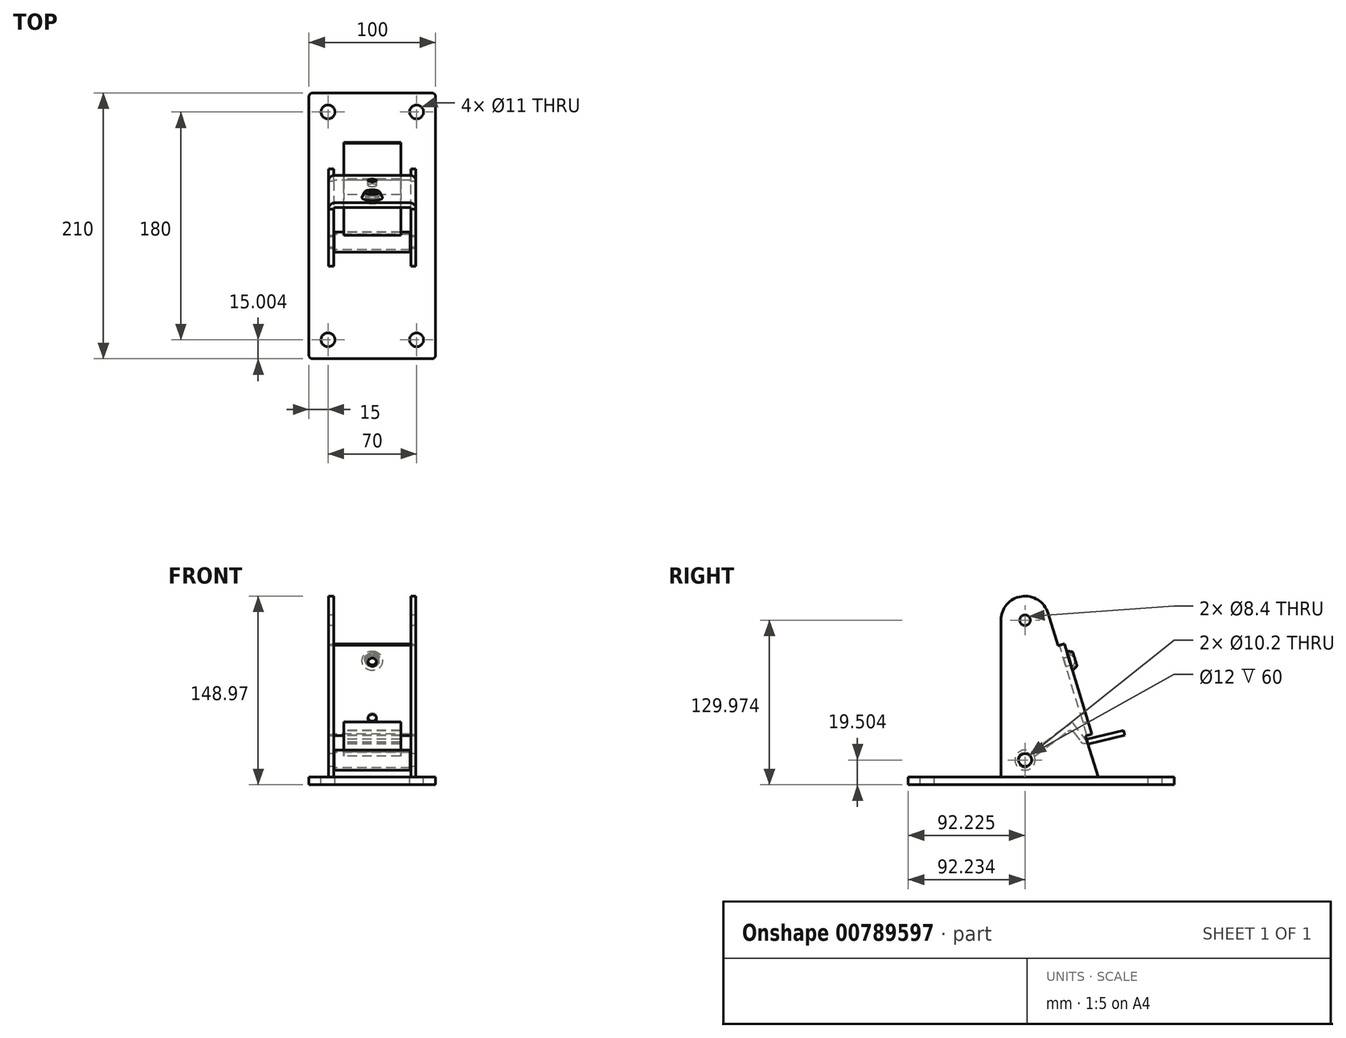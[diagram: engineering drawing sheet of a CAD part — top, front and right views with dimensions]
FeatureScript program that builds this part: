
annotation { "Feature Type Name" : "Feature", "Feature Type Description" : "" }
export const myFeature = defineFeature(function(context is Context, id is Id, definition is map)
    precondition{}
    {
        {
            var Q0;
            Q0=qCreatedBy(makeId("Right.planeOp"),FACE);
            var sketch = newSketch(context, id + "F0", { "sketchPlane" : qUnion([Q0])});
            skLineSegment(sketch, "E0", {"start": v(315.94, -407.78) * mm, "end": v(279.03, -435.24) * mm});
            skCircle(sketch, "E1", {"center": v(279.03, -435.24) * mm, "radius": 5.1 * mm});
            skLineSegment(sketch, "E2", {"start": v(281.57, -445.94) * mm, "end": v(276.5, -424.53) * mm});
            skCircle(sketch, "E3", {"center": v(279.03, -435.24) * mm, "radius": 8 * mm});
            skLineSegment(sketch, "E4", {"start": v(289.74, -432.7) * mm, "end": v(268.33, -437.77) * mm});
            skLineSegment(sketch, "E5", {"start": v(360.35, -413.08) * mm, "end": v(325.32, -421.38) * mm});
            skLineSegment(sketch, "E6", {"start": v(328.5, -424.66) * mm, "end": v(315.94, -407.78) * mm});
            skLineSegment(sketch, "E7", {"start": v(284.48, -429.5) * mm, "end": v(284.12, -427.24) * mm});
            skLineSegment(sketch, "E8", {"start": v(286.1, -431.67) * mm, "end": v(288.15, -432.66) * mm});
            skLineSegment(sketch, "E9", {"start": v(326.56, -419.78) * mm, "end": v(327.2, -423.08) * mm});
            skLineSegment(sketch, "E10", {"start": v(326.4, -420.64) * mm, "end": v(327.42, -417.44) * mm});
            skLineSegment(sketch, "E11", {"start": v(327.78, -418.75) * mm, "end": v(328.7, -422.64) * mm});
            skLineSegment(sketch, "E12", {"start": v(328.7, -422.64) * mm, "end": v(357.89, -415.72) * mm});
            skLineSegment(sketch, "E13", {"start": v(357.89, -415.72) * mm, "end": v(356.97, -411.83) * mm});
            skLineSegment(sketch, "E14", {"start": v(356.97, -411.83) * mm, "end": v(327.78, -418.75) * mm});
            skLineSegment(sketch, "E15", {"start": v(284.28, -428.88) * mm, "end": v(316.38, -405.01) * mm});
            skLineSegment(sketch, "E16", {"start": v(316.38, -405.01) * mm, "end": v(328.31, -421.06) * mm});
            skLineSegment(sketch, "E17", {"start": v(328.31, -421.06) * mm, "end": v(327.91, -421.36) * mm});
            skArc(sketch, "E18", {"start": v(327.91, -421.36) * mm, "mid": v(326.33, -415.09) * mm, "end": v(323.01, -420.64) * mm});
            skLineSegment(sketch, "E19", {"start": v(323.01, -420.64) * mm, "end": v(317.64, -413.42) * mm});
            skArc(sketch, "E20", {"start": v(317.64, -413.42) * mm, "mid": v(314.33, -418.97) * mm, "end": v(312.75, -412.7) * mm});
            skLineSegment(sketch, "E21", {"start": v(312.75, -412.7) * mm, "end": v(289.48, -430) * mm});
            skArc(sketch, "E22", {"start": v(289.48, -430) * mm, "mid": v(287.9, -423.73) * mm, "end": v(284.58, -429.29) * mm});
            skLineSegment(sketch, "E23", {"start": v(284.58, -429.29) * mm, "end": v(284.28, -428.88) * mm});
            skLineSegment(sketch, "E24", {"start": v(306.1, -423.87) * mm, "end": v(310.11, -420.89) * mm});
            skLineSegment(sketch, "E25", {"start": v(303.12, -419.86) * mm, "end": v(307.13, -416.88) * mm});
            skArc(sketch, "E26", {"start": v(307.75, -421.9) * mm, "mid": v(299.53, -415.03) * mm, "end": v(303.74, -424.88) * mm});
            skLineSegment(sketch, "E27", {"start": v(303.74, -424.88) * mm, "end": v(301.47, -421.83) * mm});
            skArc(sketch, "E28", {"start": v(301.47, -421.83) * mm, "mid": v(309.7, -428.7) * mm, "end": v(305.48, -418.85) * mm});
            skArc(sketch, "E29", {"start": v(305.48, -418.85) * mm, "mid": v(313.7, -425.72) * mm, "end": v(309.5, -415.87) * mm});
            skLineSegment(sketch, "E30", {"start": v(309.5, -415.87) * mm, "end": v(311.76, -418.91) * mm});
            skArc(sketch, "E31", {"start": v(311.76, -418.91) * mm, "mid": v(303.54, -412.05) * mm, "end": v(307.75, -421.9) * mm});
            skLineSegment(sketch, "E32", {"start": v(305.48, -418.85) * mm, "end": v(307.75, -421.9) * mm});
            skLineSegment(sketch, "E33", {"start": v(336.8, -448.74) * mm, "end": v(338.21, -446.8) * mm});
            skLineSegment(sketch, "E34", {"start": v(196.3, -454.74) * mm, "end": v(196.3, -448.74) * mm});
            skLineSegment(sketch, "E35", {"start": v(201.8, -457.66) * mm, "end": v(201.8, -445.74) * mm});
            skLineSegment(sketch, "E36", {"start": v(207.3, -454.74) * mm, "end": v(207.3, -448.74) * mm});
            skLineSegment(sketch, "E37", {"start": v(376.3, -454.74) * mm, "end": v(376.3, -448.74) * mm});
            skLineSegment(sketch, "E38", {"start": v(387.3, -454.74) * mm, "end": v(387.3, -448.74) * mm});
            skLineSegment(sketch, "E39", {"start": v(381.8, -457.66) * mm, "end": v(381.8, -445.74) * mm});
            skLineSegment(sketch, "E40", {"start": v(396.8, -454.74) * mm, "end": v(186.8, -454.74) * mm});
            skLineSegment(sketch, "E41", {"start": v(186.8, -454.74) * mm, "end": v(186.8, -448.74) * mm});
            skLineSegment(sketch, "E42", {"start": v(186.8, -448.74) * mm, "end": v(396.8, -448.74) * mm});
            skLineSegment(sketch, "E43", {"start": v(396.8, -448.74) * mm, "end": v(396.8, -454.74) * mm});
            skLineSegment(sketch, "E44", {"start": v(311.3, -454.74) * mm, "end": v(311.3, -448.74) * mm});
            skLineSegment(sketch, "E45", {"start": v(314.8, -457.66) * mm, "end": v(314.8, -445.74) * mm});
            skLineSegment(sketch, "E46", {"start": v(318.3, -454.74) * mm, "end": v(318.3, -448.74) * mm});
            skLineSegment(sketch, "E47", {"start": v(328.91, -405.14) * mm, "end": v(325.09, -406.3) * mm});
            skLineSegment(sketch, "E48", {"start": v(326.57, -397.49) * mm, "end": v(322.75, -398.66) * mm});
            skLineSegment(sketch, "E49", {"start": v(326.86, -416.22) * mm, "end": v(336.8, -448.74) * mm});
            skLineSegment(sketch, "E50", {"start": v(260.03, -448.74) * mm, "end": v(336.8, -448.74) * mm});
            skLineSegment(sketch, "E51", {"start": v(318.92, -355.35) * mm, "end": v(305.54, -359.48) * mm});
            skLineSegment(sketch, "E52", {"start": v(313.17, -353.64) * mm, "end": v(309.34, -354.81) * mm});
            skLineSegment(sketch, "E53", {"start": v(315.13, -360.05) * mm, "end": v(311.3, -361.22) * mm});
            skLineSegment(sketch, "E54", {"start": v(326.76, -398.1) * mm, "end": v(322.94, -399.28) * mm});
            skLineSegment(sketch, "E55", {"start": v(328.72, -404.52) * mm, "end": v(324.9, -405.69) * mm});
            skLineSegment(sketch, "E56", {"start": v(332.52, -399.85) * mm, "end": v(319.14, -403.94) * mm});
            skLineSegment(sketch, "E57", {"start": v(310.05, -343.46) * mm, "end": v(305.08, -344.98) * mm});
            skLineSegment(sketch, "E58", {"start": v(331.84, -414.7) * mm, "end": v(326.86, -416.22) * mm});
            skLineSegment(sketch, "E59", {"start": v(260.03, -324.77) * mm, "end": v(260.03, -448.74) * mm});
            skLineSegment(sketch, "E60", {"start": v(297.2, -319.21) * mm, "end": v(305.08, -344.98) * mm});
            skLineSegment(sketch, "E61", {"start": v(310.05, -343.46) * mm, "end": v(331.84, -414.7) * mm});
            skCircle(sketch, "E62", {"center": v(279.03, -324.77) * mm, "radius": 6.1 * mm});
            skLineSegment(sketch, "E63", {"start": v(279.03, -316.7) * mm, "end": v(279.03, -443.37) * mm});
            skLineSegment(sketch, "E64", {"start": v(287.13, -435.24) * mm, "end": v(270.93, -435.24) * mm});
            skLineSegment(sketch, "E65", {"start": v(306.23, -344.63) * mm, "end": v(328.01, -415.87) * mm});
            skLineSegment(sketch, "E66", {"start": v(287.12, -324.77) * mm, "end": v(270.92, -324.77) * mm});
            skArc(sketch, "E67", {"start": v(323.7, -445.64) * mm, "mid": v(324.47, -445.38) * mm, "end": v(324.8, -444.64) * mm});
            skArc(sketch, "E68", {"start": v(324.8, -444.64) * mm, "mid": v(324.55, -443.97) * mm, "end": v(323.9, -443.65) * mm});
            skArc(sketch, "E69", {"start": v(324.8, -418.43) * mm, "mid": v(324.51, -417.72) * mm, "end": v(323.8, -417.43) * mm});
            skArc(sketch, "E70", {"start": v(323.8, -419.43) * mm, "mid": v(324.51, -419.14) * mm, "end": v(324.8, -418.43) * mm});
            skArc(sketch, "E71", {"start": v(324.8, -421.34) * mm, "mid": v(324.55, -420.66) * mm, "end": v(323.9, -420.34) * mm});
            skArc(sketch, "E72", {"start": v(323.7, -422.33) * mm, "mid": v(324.47, -422.08) * mm, "end": v(324.8, -421.34) * mm});
            skArc(sketch, "E73", {"start": v(324.8, -424.64) * mm, "mid": v(324.55, -423.96) * mm, "end": v(323.9, -423.64) * mm});
            skArc(sketch, "E74", {"start": v(323.7, -425.63) * mm, "mid": v(324.47, -425.38) * mm, "end": v(324.8, -424.64) * mm});
            skArc(sketch, "E75", {"start": v(324.8, -427.94) * mm, "mid": v(324.55, -427.26) * mm, "end": v(323.9, -426.94) * mm});
            skArc(sketch, "E76", {"start": v(323.7, -428.93) * mm, "mid": v(324.47, -428.68) * mm, "end": v(324.8, -427.94) * mm});
            skArc(sketch, "E77", {"start": v(324.8, -431.24) * mm, "mid": v(324.55, -430.56) * mm, "end": v(323.9, -430.24) * mm});
            skArc(sketch, "E78", {"start": v(323.7, -432.23) * mm, "mid": v(324.47, -431.98) * mm, "end": v(324.8, -431.24) * mm});
            skArc(sketch, "E79", {"start": v(324.8, -434.54) * mm, "mid": v(324.55, -433.86) * mm, "end": v(323.9, -433.54) * mm});
            skArc(sketch, "E80", {"start": v(323.7, -435.53) * mm, "mid": v(324.47, -435.28) * mm, "end": v(324.8, -434.54) * mm});
            skArc(sketch, "E81", {"start": v(324.8, -437.84) * mm, "mid": v(324.55, -437.16) * mm, "end": v(323.9, -436.84) * mm});
            skArc(sketch, "E82", {"start": v(323.7, -438.83) * mm, "mid": v(324.47, -438.58) * mm, "end": v(324.8, -437.84) * mm});
            skArc(sketch, "E83", {"start": v(324.8, -441.14) * mm, "mid": v(324.55, -440.46) * mm, "end": v(323.9, -440.14) * mm});
            skArc(sketch, "E84", {"start": v(323.7, -442.13) * mm, "mid": v(324.47, -441.88) * mm, "end": v(324.8, -441.14) * mm});
            skArc(sketch, "E85", {"start": v(324.8, -447.74) * mm, "mid": v(324.51, -447.03) * mm, "end": v(323.8, -446.74) * mm});
            skArc(sketch, "E86", {"start": v(323.8, -448.74) * mm, "mid": v(324.51, -448.44) * mm, "end": v(324.8, -447.74) * mm});
            skLineSegment(sketch, "E87", {"start": v(323.7, -432.23) * mm, "end": v(305.7, -430.43) * mm});
            skLineSegment(sketch, "E88", {"start": v(313.46, -446.74) * mm, "end": v(319.06, -445.17) * mm});
            skLineSegment(sketch, "E89", {"start": v(319.77, -446.74) * mm, "end": v(323.7, -445.64) * mm});
            skArc(sketch, "E90", {"start": v(313.98, -448.74) * mm, "mid": v(313.85, -449.23) * mm, "end": v(313.8, -449.74) * mm});
            skArc(sketch, "E91", {"start": v(316.8, -448.74) * mm, "mid": v(316.1, -449.03) * mm, "end": v(315.8, -449.74) * mm});
            skLineSegment(sketch, "E92", {"start": v(316.8, -448.74) * mm, "end": v(323.8, -448.74) * mm});
            skArc(sketch, "E93", {"start": v(305.9, -418.54) * mm, "mid": v(305.13, -418.8) * mm, "end": v(304.8, -419.54) * mm});
            skArc(sketch, "E94", {"start": v(304.8, -419.54) * mm, "mid": v(305.06, -420.2) * mm, "end": v(305.7, -420.53) * mm});
            skArc(sketch, "E95", {"start": v(305.9, -421.84) * mm, "mid": v(305.13, -422.1) * mm, "end": v(304.8, -422.84) * mm});
            skArc(sketch, "E96", {"start": v(304.8, -422.84) * mm, "mid": v(305.06, -423.5) * mm, "end": v(305.7, -423.83) * mm});
            skArc(sketch, "E97", {"start": v(305.9, -425.14) * mm, "mid": v(305.13, -425.4) * mm, "end": v(304.8, -426.14) * mm});
            skArc(sketch, "E98", {"start": v(304.8, -426.14) * mm, "mid": v(305.06, -426.8) * mm, "end": v(305.7, -427.13) * mm});
            skArc(sketch, "E99", {"start": v(305.9, -428.44) * mm, "mid": v(305.13, -428.7) * mm, "end": v(304.8, -429.44) * mm});
            skArc(sketch, "E100", {"start": v(304.8, -429.44) * mm, "mid": v(305.06, -430.1) * mm, "end": v(305.7, -430.43) * mm});
            skArc(sketch, "E101", {"start": v(305.9, -431.74) * mm, "mid": v(305.13, -432) * mm, "end": v(304.8, -432.74) * mm});
            skArc(sketch, "E102", {"start": v(304.8, -432.74) * mm, "mid": v(305.06, -433.4) * mm, "end": v(305.7, -433.73) * mm});
            skArc(sketch, "E103", {"start": v(305.9, -435.04) * mm, "mid": v(305.13, -435.3) * mm, "end": v(304.8, -436.04) * mm});
            skArc(sketch, "E104", {"start": v(304.8, -436.04) * mm, "mid": v(305.06, -436.7) * mm, "end": v(305.7, -437.03) * mm});
            skArc(sketch, "E105", {"start": v(304.8, -439.34) * mm, "mid": v(305.06, -440) * mm, "end": v(305.7, -440.33) * mm});
            skArc(sketch, "E106", {"start": v(305.9, -438.34) * mm, "mid": v(305.13, -438.6) * mm, "end": v(304.8, -439.34) * mm});
            skArc(sketch, "E107", {"start": v(304.8, -447.74) * mm, "mid": v(305.1, -448.44) * mm, "end": v(305.8, -448.74) * mm});
            skArc(sketch, "E108", {"start": v(305.8, -446.74) * mm, "mid": v(305.1, -447.03) * mm, "end": v(304.8, -447.74) * mm});
            skArc(sketch, "E109", {"start": v(304.8, -442.84) * mm, "mid": v(305.06, -443.51) * mm, "end": v(305.7, -443.84) * mm});
            skArc(sketch, "E110", {"start": v(305.9, -441.85) * mm, "mid": v(305.13, -442.1) * mm, "end": v(304.8, -442.84) * mm});
            skLineSegment(sketch, "E111", {"start": v(318.16, -419.77) * mm, "end": v(323.8, -419.43) * mm});
            skLineSegment(sketch, "E112", {"start": v(305.9, -418.54) * mm, "end": v(314.8, -417.93) * mm});
            skLineSegment(sketch, "E113", {"start": v(323.7, -422.33) * mm, "end": v(305.7, -420.53) * mm});
            skLineSegment(sketch, "E114", {"start": v(323.9, -420.34) * mm, "end": v(305.9, -418.54) * mm});
            skLineSegment(sketch, "E115", {"start": v(323.7, -425.63) * mm, "end": v(305.7, -423.83) * mm});
            skLineSegment(sketch, "E116", {"start": v(323.9, -423.64) * mm, "end": v(305.9, -421.84) * mm});
            skLineSegment(sketch, "E117", {"start": v(323.7, -428.93) * mm, "end": v(305.7, -427.13) * mm});
            skLineSegment(sketch, "E118", {"start": v(323.9, -426.94) * mm, "end": v(305.9, -425.14) * mm});
            skLineSegment(sketch, "E119", {"start": v(323.9, -430.24) * mm, "end": v(305.9, -428.44) * mm});
            skLineSegment(sketch, "E120", {"start": v(323.7, -435.53) * mm, "end": v(305.7, -433.73) * mm});
            skLineSegment(sketch, "E121", {"start": v(323.9, -433.54) * mm, "end": v(305.9, -431.74) * mm});
            skLineSegment(sketch, "E122", {"start": v(323.7, -438.83) * mm, "end": v(305.7, -437.03) * mm});
            skLineSegment(sketch, "E123", {"start": v(323.9, -436.84) * mm, "end": v(305.9, -435.04) * mm});
            skLineSegment(sketch, "E124", {"start": v(323.9, -440.14) * mm, "end": v(305.9, -438.34) * mm});
            skLineSegment(sketch, "E125", {"start": v(323.7, -442.13) * mm, "end": v(305.7, -440.33) * mm});
            skLineSegment(sketch, "E126", {"start": v(314.8, -417.43) * mm, "end": v(314.8, -419.43) * mm});
            skLineSegment(sketch, "E127", {"start": v(314.8, -419.43) * mm, "end": v(323.8, -419.43) * mm});
            skLineSegment(sketch, "E128", {"start": v(305.8, -446.74) * mm, "end": v(323.8, -446.74) * mm});
            skLineSegment(sketch, "E129", {"start": v(323.7, -445.64) * mm, "end": v(305.7, -443.84) * mm});
            skLineSegment(sketch, "E130", {"start": v(323.9, -443.65) * mm, "end": v(305.9, -441.85) * mm});
            skLineSegment(sketch, "E131", {"start": v(313.8, -454.74) * mm, "end": v(315.8, -454.74) * mm});
            skLineSegment(sketch, "E132", {"start": v(315.8, -449.74) * mm, "end": v(315.8, -454.74) * mm});
            skLineSegment(sketch, "E133", {"start": v(313.8, -449.74) * mm, "end": v(313.8, -454.74) * mm});
            skLineSegment(sketch, "E134", {"start": v(305.8, -448.74) * mm, "end": v(323.8, -448.74) * mm});
            skLineSegment(sketch, "E135", {"start": v(314.8, -417.43) * mm, "end": v(323.8, -417.43) * mm});
            skLineSegment(sketch, "E136", {"start": v(305.72, -421.84) * mm, "end": v(312.85, -421.25) * mm});
            skLineSegment(sketch, "E137", {"start": v(316.76, -422.93) * mm, "end": v(323.89, -422.33) * mm});
            skLineSegment(sketch, "E138", {"start": v(305.72, -425.14) * mm, "end": v(312.85, -424.55) * mm});
            skLineSegment(sketch, "E139", {"start": v(316.76, -426.23) * mm, "end": v(323.89, -425.63) * mm});
            skLineSegment(sketch, "E140", {"start": v(305.72, -428.44) * mm, "end": v(312.85, -427.85) * mm});
            skLineSegment(sketch, "E141", {"start": v(316.76, -429.53) * mm, "end": v(323.89, -428.93) * mm});
            skLineSegment(sketch, "E142", {"start": v(305.72, -431.74) * mm, "end": v(312.85, -431.15) * mm});
            skLineSegment(sketch, "E143", {"start": v(316.76, -432.83) * mm, "end": v(323.89, -432.23) * mm});
            skLineSegment(sketch, "E144", {"start": v(305.72, -435.04) * mm, "end": v(312.85, -434.45) * mm});
            skLineSegment(sketch, "E145", {"start": v(316.76, -436.13) * mm, "end": v(323.89, -435.53) * mm});
            skLineSegment(sketch, "E146", {"start": v(305.72, -438.34) * mm, "end": v(312.85, -437.75) * mm});
            skLineSegment(sketch, "E147", {"start": v(316.76, -439.43) * mm, "end": v(323.89, -438.83) * mm});
            skLineSegment(sketch, "E148", {"start": v(316.12, -442.87) * mm, "end": v(323.9, -442.13) * mm});
            skLineSegment(sketch, "E149", {"start": v(305.7, -441.85) * mm, "end": v(313.48, -441.1) * mm});
            skLineSegment(sketch, "E150", {"start": v(279.03, -443.24) * mm, "end": v(279.03, -427.24) * mm});
            skCircle(sketch, "E151", {"center": v(279.03, -435.24) * mm, "radius": 5 * mm});
            skLineSegment(sketch, "E152", {"start": v(271.03, -435.24) * mm, "end": v(287.03, -435.24) * mm});
            skLineSegment(sketch, "E153", {"start": v(283.78, -433.65) * mm, "end": v(284.73, -433.1) * mm});
            skArc(sketch, "E154", {"start": v(284.73, -433.1) * mm, "mid": v(285.1, -431.74) * mm, "end": v(283.73, -431.37) * mm});
            skLineSegment(sketch, "E155", {"start": v(283.73, -431.37) * mm, "end": v(282.78, -431.92) * mm});
            skLineSegment(sketch, "E156", {"start": v(282.78, -438.55) * mm, "end": v(283.73, -439.1) * mm});
            skArc(sketch, "E157", {"start": v(283.73, -439.1) * mm, "mid": v(285.1, -438.74) * mm, "end": v(284.73, -437.37) * mm});
            skLineSegment(sketch, "E158", {"start": v(284.73, -437.37) * mm, "end": v(283.78, -436.82) * mm});
            skLineSegment(sketch, "E159", {"start": v(278.03, -440.13) * mm, "end": v(278.03, -441.24) * mm});
            skArc(sketch, "E160", {"start": v(278.03, -441.24) * mm, "mid": v(279.03, -442.24) * mm, "end": v(280.03, -441.24) * mm});
            skLineSegment(sketch, "E161", {"start": v(280.03, -441.24) * mm, "end": v(280.03, -440.13) * mm});
            skLineSegment(sketch, "E162", {"start": v(274.3, -436.82) * mm, "end": v(273.34, -437.37) * mm});
            skArc(sketch, "E163", {"start": v(273.34, -437.37) * mm, "mid": v(272.97, -438.74) * mm, "end": v(274.34, -439.1) * mm});
            skLineSegment(sketch, "E164", {"start": v(274.34, -439.1) * mm, "end": v(275.3, -438.55) * mm});
            skLineSegment(sketch, "E165", {"start": v(275.3, -431.92) * mm, "end": v(274.34, -431.37) * mm});
            skArc(sketch, "E166", {"start": v(274.34, -431.37) * mm, "mid": v(272.97, -431.74) * mm, "end": v(273.34, -433.1) * mm});
            skLineSegment(sketch, "E167", {"start": v(273.34, -433.1) * mm, "end": v(274.3, -433.65) * mm});
            skLineSegment(sketch, "E168", {"start": v(280.03, -430.34) * mm, "end": v(280.03, -429.24) * mm});
            skArc(sketch, "E169", {"start": v(280.03, -429.24) * mm, "mid": v(279.03, -428.24) * mm, "end": v(278.03, -429.24) * mm});
            skLineSegment(sketch, "E170", {"start": v(278.03, -429.24) * mm, "end": v(278.03, -430.34) * mm});
            skArc(sketch, "E171", {"start": v(275.3, -438.55) * mm, "mid": v(276.53, -439.57) * mm, "end": v(278.03, -440.13) * mm});
            skArc(sketch, "E172", {"start": v(274.3, -433.65) * mm, "mid": v(274.03, -435.24) * mm, "end": v(274.3, -436.82) * mm});
            skArc(sketch, "E173", {"start": v(278.03, -430.34) * mm, "mid": v(276.53, -430.9) * mm, "end": v(275.3, -431.92) * mm});
            skArc(sketch, "E174", {"start": v(282.78, -431.92) * mm, "mid": v(281.53, -430.9) * mm, "end": v(280.03, -430.34) * mm});
            skArc(sketch, "E175", {"start": v(283.78, -436.82) * mm, "mid": v(284.03, -435.24) * mm, "end": v(283.78, -433.65) * mm});
            skArc(sketch, "E176", {"start": v(280.03, -440.13) * mm, "mid": v(281.53, -439.57) * mm, "end": v(282.78, -438.55) * mm});
            skCircle(sketch, "E177", {"center": v(279.03, -435.24) * mm, "radius": 6 * mm});
            skCircle(sketch, "E178", {"center": v(279.03, -435.24) * mm, "radius": 10 * mm});
            skLineSegment(sketch, "E179", {"start": v(279.03, -333.77) * mm, "end": v(279.03, -315.77) * mm});
            skCircle(sketch, "E180", {"center": v(279.03, -324.77) * mm, "radius": 4 * mm});
            skCircle(sketch, "E181", {"center": v(279.03, -324.77) * mm, "radius": 6 * mm});
            skLineSegment(sketch, "E182", {"start": v(270.03, -324.77) * mm, "end": v(288.03, -324.77) * mm});
            skCircle(sketch, "E183", {"center": v(279.02, -324.77) * mm, "radius": 8 * mm});
            skCircle(sketch, "E184", {"center": v(279.02, -324.77) * mm, "radius": 4.2 * mm});
            skCircle(sketch, "E185", {"center": v(279.03, -324.77) * mm, "radius": 9 * mm});
            skArc(sketch, "E186", {"start": v(279.03, -320.77) * mm, "mid": v(276.2, -327.6) * mm, "end": v(283.03, -324.77) * mm});
            skCircle(sketch, "E187", {"center": v(279.03, -324.77) * mm, "radius": 3.15 * mm});
            skCircle(sketch, "E188", {"center": v(279.03, -324.77) * mm, "radius": 6.5 * mm});
            skCircle(sketch, "E189", {"center": v(279.03, -324.77) * mm, "radius": 4.5 * mm});
            skCircle(sketch, "E190", {"center": v(279.03, -324.77) * mm, "radius": 3.5 * mm});
            skCircle(sketch, "E191", {"center": v(312.54, -67.54) * mm, "radius": 8 * mm});
            skCircle(sketch, "E192", {"center": v(312.54, -67.54) * mm, "radius": 9 * mm});
            skCircle(sketch, "E193", {"center": v(312.54, -67.54) * mm, "radius": 12 * mm});
            skLineSegment(sketch, "E194", {"start": v(324.54, -67.54) * mm, "end": v(300.54, -67.54) * mm});
            skLineSegment(sketch, "E195", {"start": v(312.54, -79.54) * mm, "end": v(312.54, -55.54) * mm});
            skFitSpline(sketch, "E196", {"points": [v(83.93, 382.11) * mm, v(84.32, 380.72) * mm, v(89.43, 363.27) * mm, v(105.35, 319.17) * mm, v(124.1, 270.52) * mm, v(146.38, 223.76) * mm, v(158.35, 173.5) * mm, v(157.13, 123.1) * mm, v(158.1, 75.33) * mm, v(160.73, 43.74) * mm, v(168.5, 18.56) * mm]});
            skFitSpline(sketch, "E197", {"points": [v(119.52, 379.69) * mm, v(124.73, 363.72) * mm, v(139.09, 321.83) * mm, v(153.67, 273.63) * mm, v(167.42, 224.72) * mm, v(171.42, 174.5) * mm, v(173.76, 124.08) * mm, v(168.44, 76.4) * mm, v(163.57, 44.35) * mm, v(169.3, 17.5) * mm]});
            skFitSpline(sketch, "E198", {"points": [v(133.07, 384.14) * mm, v(133.82, 381.98) * mm, v(134.58, 379.8) * mm, v(140.17, 358.65) * mm, v(141.75, 354.28) * mm, v(144.85, 345.7) * mm, v(146.37, 341.5) * mm, v(148.9, 334.42) * mm, v(149.91, 331.55) * mm, v(151.87, 325.89) * mm, v(152.81, 323.1) * mm, v(154.67, 317.53) * mm, v(155.58, 314.74) * mm, v(158.4, 305.95) * mm, v(160.26, 299.94) * mm, v(163.44, 289.43) * mm, v(164.77, 284.94) * mm, v(167.05, 277.16) * mm, v(168, 273.88) * mm, v(169.9, 267.27) * mm, v(170.85, 263.94) * mm, v(173.6, 253.9) * mm, v(175.34, 247.1) * mm, v(177.85, 235.94) * mm, v(178.74, 231.63) * mm, v(180.17, 223.67) * mm, v(180.75, 220.06) * mm, v(181.77, 212.85) * mm, v(182.22, 209.25) * mm, v(183.41, 198.5) * mm, v(184.01, 191.35) * mm, v(184.73, 181.35) * mm, v(184.92, 178.46) * mm, v(185.28, 172.67) * mm, v(185.46, 169.77) * mm, v(185.78, 163.96) * mm, v(185.93, 161.04) * mm, v(186.32, 152.27) * mm, v(186.51, 146.4) * mm, v(186.64, 135.73) * mm, v(186.62, 130.95) * mm, v(186.45, 123.84) * mm, v(186.36, 121.52) * mm, v(186.15, 116.89) * mm, v(186.02, 114.58) * mm, v(185.58, 107.67) * mm, v(185.2, 103.09) * mm, v(184.35, 94.2) * mm, v(183.88, 89.88) * mm, v(183, 82.43) * mm, v(182.61, 79.29) * mm, v(182.01, 74.66) * mm, v(181.82, 73.17) * mm, v(181.42, 70.2) * mm, v(181.22, 68.72) * mm, v(180.83, 65.8) * mm, v(180.64, 64.35) * mm, v(179.95, 58.96) * mm, v(179.51, 55.12) * mm, v(178.95, 47.67) * mm, v(178.82, 44.08) * mm, v(179, 37.18) * mm, v(179.3, 33.87) * mm, v(179.9, 30.55) * mm, v(179.93, 30.41) * mm, v(182.32, 19.73) * mm]});
            skFitSpline(sketch, "E199", {"points": [v(97.76, 388.42) * mm, v(98.4, 386.46) * mm, v(99.68, 382.6) * mm, v(102.46, 374.34) * mm, v(107.26, 355.3) * mm, v(110.8, 345.28) * mm, v(112.85, 339.66) * mm, v(116.76, 329.06) * mm, v(118.62, 324.09) * mm, v(122.37, 314.17) * mm, v(124.25, 309.23) * mm, v(128.08, 299.4) * mm, v(130.02, 294.51) * mm, v(133.53, 285.9) * mm, v(135.09, 282.16) * mm, v(137.65, 276.13) * mm, v(138.65, 273.83) * mm, v(140.68, 269.2) * mm, v(141.71, 266.86) * mm, v(144.82, 259.83) * mm, v(146.91, 255.1) * mm, v(150.6, 246.49) * mm, v(152.2, 242.64) * mm, v(154.93, 235.8) * mm, v(156.07, 232.81) * mm, v(158.16, 227.03) * mm, v(159.12, 224.24) * mm, v(160.94, 218.61) * mm, v(161.8, 215.78) * mm, v(164.36, 206.83) * mm, v(165.86, 200.64) * mm, v(168.03, 189.8) * mm, v(168.8, 185.17) * mm, v(169.9, 176.95) * mm, v(170.28, 173.37) * mm, v(170.87, 166.26) * mm, v(171.08, 162.72) * mm, v(171.61, 150.12) * mm, v(171.59, 141.2) * mm, v(171.53, 129.97) * mm, v(171.52, 127.49) * mm, v(171.5, 123.08) * mm, v(171.5, 121.14) * mm, v(171.5, 117.27) * mm, v(171.52, 115.33) * mm, v(171.56, 109.53) * mm, v(171.61, 105.67) * mm, v(171.85, 94.1) * mm, v(172.12, 86.42) * mm, v(172.66, 76.03) * mm, v(172.82, 73.32) * mm, v(173.18, 67.94) * mm, v(173.38, 65.28) * mm, v(173.85, 60.01) * mm, v(174.12, 57.4) * mm, v(175.07, 49.7) * mm, v(175.9, 44.69) * mm, v(177.94, 35.72) * mm, v(179.07, 31.72) * mm, v(182.32, 19.73) * mm]});
            skLineSegment(sketch, "E200", {"start": v(180.51, 18) * mm, "end": v(170.58, 17.16) * mm});
            skArc(sketch, "E201", {"start": v(168.5, 18.56) * mm, "mid": v(169.3, 17.5) * mm, "end": v(170.58, 17.16) * mm});
            skArc(sketch, "E202", {"start": v(180.51, 18) * mm, "mid": v(181.72, 18.55) * mm, "end": v(182.32, 19.73) * mm});
            skLineSegment(sketch, "E203", {"start": v(114.48, 393.57) * mm, "end": v(85.26, 384.57) * mm});
            skArc(sketch, "E204", {"start": v(133.07, 384.14) * mm, "mid": v(125.68, 392.61) * mm, "end": v(114.48, 393.57) * mm});
            skArc(sketch, "E205", {"start": v(119.52, 379.69) * mm, "mid": v(112.16, 388.35) * mm, "end": v(100.84, 389.37) * mm});
            skArc(sketch, "E206", {"start": v(85.26, 384.57) * mm, "mid": v(84.1, 383.61) * mm, "end": v(83.93, 382.11) * mm});
            skLineSegment(sketch, "E207", {"start": v(152.57, 132.45) * mm, "end": v(191.6, 135.82) * mm});
            skLineSegment(sketch, "E208", {"start": v(158.6, 36.16) * mm, "end": v(184, 38.35) * mm});
            skLineSegment(sketch, "E209", {"start": v(237.92, -255.81) * mm, "end": v(274.24, -244.63) * mm});
            skArc(sketch, "E210", {"start": v(236.67, -255.15) * mm, "mid": v(237.16, -255.74) * mm, "end": v(237.92, -255.81) * mm});
            skArc(sketch, "E211", {"start": v(274.24, -244.63) * mm, "mid": v(274.83, -244.14) * mm, "end": v(274.9, -243.38) * mm});
            skLineSegment(sketch, "E212", {"start": v(238.95, -252.36) * mm, "end": v(271.44, -242.35) * mm});
            skLineSegment(sketch, "E213", {"start": v(226.15, -217.59) * mm, "end": v(262.46, -206.4) * mm});
            skLineSegment(sketch, "E214", {"start": v(228.94, -219.86) * mm, "end": v(261.43, -209.86) * mm});
            skLineSegment(sketch, "E215", {"start": v(225.48, -218.84) * mm, "end": v(236.67, -255.15) * mm});
            skArc(sketch, "E216", {"start": v(226.15, -217.59) * mm, "mid": v(225.56, -218.07) * mm, "end": v(225.48, -218.84) * mm});
            skLineSegment(sketch, "E217", {"start": v(228.94, -219.86) * mm, "end": v(238.95, -252.36) * mm});
            skLineSegment(sketch, "E218", {"start": v(263.71, -207.06) * mm, "end": v(274.9, -243.38) * mm});
            skArc(sketch, "E219", {"start": v(263.71, -207.06) * mm, "mid": v(263.22, -206.47) * mm, "end": v(262.46, -206.4) * mm});
            skLineSegment(sketch, "E220", {"start": v(261.43, -209.86) * mm, "end": v(271.44, -242.35) * mm});
            skLineSegment(sketch, "E221", {"start": v(232.18, -257.58) * mm, "end": v(218.98, -214.7) * mm});
            skArc(sketch, "E222", {"start": v(232.18, -257.58) * mm, "mid": v(234.62, -260.53) * mm, "end": v(238.43, -260.89) * mm});
            skLineSegment(sketch, "E223", {"start": v(163.65, 143.24) * mm, "end": v(158.88, 26.97) * mm});
            skLineSegment(sketch, "E224", {"start": v(168.65, 143.06) * mm, "end": v(163.87, 26.79) * mm});
            skLineSegment(sketch, "E225", {"start": v(158.88, 26.97) * mm, "end": v(163.87, 26.79) * mm});
            skLineSegment(sketch, "E226", {"start": v(168.65, 143.06) * mm, "end": v(163.65, 143.24) * mm});
            skArc(sketch, "E227", {"start": v(274.41, -249.8) * mm, "mid": v(275.41, -249.37) * mm, "end": v(276.3, -248.73) * mm});
            skArc(sketch, "E228", {"start": v(186.4, 128.3) * mm, "mid": v(180.4, 139.13) * mm, "end": v(168.65, 143.06) * mm});
            skArc(sketch, "E229", {"start": v(186.4, 128.3) * mm, "mid": v(194.6, 61.33) * mm, "end": v(208.63, -4.66) * mm});
            skArc(sketch, "E230", {"start": v(208.63, -4.66) * mm, "mid": v(218.95, -21) * mm, "end": v(236.37, -29.37) * mm});
            skArc(sketch, "E231", {"start": v(218.94, -211.96) * mm, "mid": v(224.25, -125.4) * mm, "end": v(177.3, -52.5) * mm});
            skArc(sketch, "E232", {"start": v(218.94, -211.96) * mm, "mid": v(218.76, -213.33) * mm, "end": v(218.98, -214.7) * mm});
            skLineSegment(sketch, "E233", {"start": v(163.87, 26.79) * mm, "end": v(162.53, -20.31) * mm});
            skCircle(sketch, "E234", {"center": v(312.54, -67.54) * mm, "radius": 9.15 * mm});
            skLineSegment(sketch, "E235", {"start": v(302.3, -57.78) * mm, "end": v(322.78, -77.3) * mm});
            skLineSegment(sketch, "E236", {"start": v(322.3, -57.3) * mm, "end": v(302.77, -77.79) * mm});
            skCircle(sketch, "E237", {"center": v(297.32, -54.81) * mm, "radius": 5 * mm});
            skCircle(sketch, "E238", {"center": v(326.22, -78.1) * mm, "radius": 5 * mm});
            skLineSegment(sketch, "E239", {"start": v(238.43, -260.89) * mm, "end": v(274.41, -249.8) * mm});
            skArc(sketch, "E240", {"start": v(341.24, -84.3) * mm, "mid": v(328.62, -55.4) * mm, "end": v(300.92, -40.32) * mm});
            skLineSegment(sketch, "E241", {"start": v(236.37, -29.37) * mm, "end": v(300.92, -40.32) * mm});
            skArc(sketch, "E242", {"start": v(276.3, -248.73) * mm, "mid": v(327.93, -174.08) * mm, "end": v(341.24, -84.3) * mm});
            skArc(sketch, "E243", {"start": v(162.53, -20.31) * mm, "mid": v(166.16, -38.13) * mm, "end": v(177.3, -52.5) * mm});
            skLineSegment(sketch, "E244", {"start": v(162.35, 133.31) * mm, "end": v(169.14, 133.03) * mm});
            skLineSegment(sketch, "E245", {"start": v(158.39, 36.89) * mm, "end": v(165.17, 36.6) * mm});
            skLineSegment(sketch, "E246", {"start": v(291.63, -423.43) * mm, "end": v(239.83, -255.22) * mm});
            skLineSegment(sketch, "E247", {"start": v(324.12, -413.42) * mm, "end": v(272.32, -245.22) * mm});
            skCircle(sketch, "E248", {"center": v(279.03, -324.77) * mm, "radius": 6.05 * mm});
            skLineSegment(sketch, "E249", {"start": v(288.73, -321.78) * mm, "end": v(269.33, -327.75) * mm});
            skLineSegment(sketch, "E250", {"start": v(288.76, -424.31) * mm, "end": v(236.96, -256.1) * mm});
            skLineSegment(sketch, "E251", {"start": v(236.96, -256.1) * mm, "end": v(275.2, -244.33) * mm});
            skLineSegment(sketch, "E252", {"start": v(275.2, -244.33) * mm, "end": v(327, -412.54) * mm});
            skLineSegment(sketch, "E253", {"start": v(327, -412.54) * mm, "end": v(288.76, -424.31) * mm});
            skLineSegment(sketch, "E254", {"start": v(312.54, -67.54) * mm, "end": v(310.98, -102.75) * mm});
            skLineSegment(sketch, "E255", {"start": v(312.54, -67.54) * mm, "end": v(277.3, -67.61) * mm});
            skLineSegment(sketch, "E256", {"start": v(322.78, -77.3) * mm, "end": v(302.3, -57.78) * mm});
            skArc(sketch, "E257", {"start": v(299.08, -78.2) * mm, "mid": v(299.1, -75.6) * mm, "end": v(296.79, -74.4) * mm});
            skArc(sketch, "E258", {"start": v(336.26, -84.7) * mm, "mid": v(324.93, -58.78) * mm, "end": v(300.08, -45.25) * mm});
            skArc(sketch, "E259", {"start": v(301.29, -111.3) * mm, "mid": v(310.62, -112.68) * mm, "end": v(320.04, -112.09) * mm});
            skArc(sketch, "E260", {"start": v(300.54, -110.32) * mm, "mid": v(300.75, -110.94) * mm, "end": v(301.29, -111.3) * mm});
            skArc(sketch, "E261", {"start": v(320.04, -112.09) * mm, "mid": v(332.29, -104.92) * mm, "end": v(336.7, -91.42) * mm});
            skArc(sketch, "E262", {"start": v(295.46, -69.4) * mm, "mid": v(295.94, -71.95) * mm, "end": v(296.79, -74.4) * mm});
            skArc(sketch, "E263", {"start": v(299.08, -78.2) * mm, "mid": v(305.2, -83.07) * mm, "end": v(312.85, -84.71) * mm});
            skArc(sketch, "E264", {"start": v(295.46, -69.4) * mm, "mid": v(289.17, -61.43) * mm, "end": v(279.46, -64.4) * mm});
            skArc(sketch, "E265", {"start": v(277.72, -63.49) * mm, "mid": v(278.21, -64.66) * mm, "end": v(279.46, -64.4) * mm});
            skArc(sketch, "E266", {"start": v(336.7, -91.42) * mm, "mid": v(336.5, -88.06) * mm, "end": v(336.26, -84.7) * mm});
            skLineSegment(sketch, "E267", {"start": v(300.08, -45.25) * mm, "end": v(294.12, -44.24) * mm});
            skLineSegment(sketch, "E268", {"start": v(300.54, -110.32) * mm, "end": v(300.54, -102) * mm});
            skArc(sketch, "E269", {"start": v(290.22, -45.22) * mm, "mid": v(282.54, -53.38) * mm, "end": v(277.72, -63.49) * mm});
            skArc(sketch, "E270", {"start": v(294.12, -44.24) * mm, "mid": v(292.07, -44.32) * mm, "end": v(290.22, -45.22) * mm});
            skArc(sketch, "E271", {"start": v(314.94, -102.63) * mm, "mid": v(319.66, -100.9) * mm, "end": v(322.72, -96.92) * mm});
            skArc(sketch, "E272", {"start": v(319.4, -87.36) * mm, "mid": v(316.4, -85.37) * mm, "end": v(312.85, -84.71) * mm});
            skArc(sketch, "E273", {"start": v(322.72, -96.92) * mm, "mid": v(329.08, -89.36) * mm, "end": v(319.4, -87.36) * mm});
            skArc(sketch, "E274", {"start": v(301.84, -101.05) * mm, "mid": v(308.32, -102.46) * mm, "end": v(314.94, -102.63) * mm});
            skArc(sketch, "E275", {"start": v(301.84, -101.05) * mm, "mid": v(300.95, -101.2) * mm, "end": v(300.54, -102) * mm});
            skFitSpline(sketch, "E276", {"points": [v(207, -32.32) * mm, v(216.03, -34.52) * mm, v(243.28, -36.57) * mm, v(284.13, -29.33) * mm, v(334.26, -25.3) * mm, v(383.86, -19.5) * mm, v(433.52, -13.28) * mm, v(483.46, -10.52) * mm, v(525, -6.98) * mm, v(549.97, -4.46) * mm, v(556.96, -4.51) * mm]});
            skFitSpline(sketch, "E277", {"points": [v(208.47, -36.1) * mm, v(217.08, -39.32) * mm, v(243.69, -45.56) * mm, v(285.6, -48.73) * mm, v(336.07, -45.2) * mm, v(385.62, -38.57) * mm, v(435.09, -30.54) * mm, v(484.46, -21.9) * mm, v(525.37, -15.51) * mm, v(557.77, -9.17) * mm, v(617.36, -22.3) * mm]});
            skFitSpline(sketch, "E278", {"points": [v(208.41, -18.65) * mm, v(211.17, -19.36) * mm, v(214.08, -19.91) * mm, v(221.74, -20.69) * mm, v(225.33, -20.97) * mm, v(231.2, -21.17) * mm, v(233.45, -21.19) * mm, v(242.15, -21.06) * mm, v(248.57, -20.55) * mm, v(261.58, -19.1) * mm, v(268.17, -18.16) * mm, v(276.92, -16.96) * mm, v(278.92, -16.69) * mm, v(282.93, -16.16) * mm, v(284.95, -15.9) * mm, v(288.99, -15.42) * mm, v(291, -15.2) * mm, v(297.05, -14.52) * mm, v(301.08, -14.1) * mm, v(313.12, -12.92) * mm, v(321.1, -12.2) * mm, v(332.19, -11.14) * mm, v(335.35, -10.83) * mm, v(341.67, -10.18) * mm, v(344.84, -9.84) * mm, v(354.32, -8.81) * mm, v(360.65, -8.1) * mm, v(373.42, -6.6) * mm, v(379.86, -5.82) * mm, v(392.78, -4.25) * mm, v(399.27, -3.45) * mm, v(410.62, -2.14) * mm, v(415.45, -1.6) * mm, v(423.58, -0.74) * mm, v(426.85, -0.42) * mm, v(433.23, 0.18) * mm, v(436.32, 0.44) * mm, v(442.5, 0.95) * mm, v(445.57, 1.18) * mm, v(454.79, 1.85) * mm, v(460.9, 2.26) * mm, v(471.85, 2.97) * mm, v(476.7, 3.3) * mm, v(484.42, 3.83) * mm, v(487.32, 4.04) * mm, v(493.12, 4.47) * mm, v(496.02, 4.69) * mm, v(504.76, 5.35) * mm, v(510.6, 5.8) * mm, v(519.83, 6.46) * mm, v(523.18, 6.7) * mm, v(530.13, 7.15) * mm, v(533.74, 7.37) * mm, v(539.07, 7.67) * mm, v(540.8, 7.76) * mm, v(544, 7.93) * mm, v(545.47, 8) * mm, v(549.38, 8.2) * mm, v(551.84, 8.32) * mm, v(555.14, 8.47) * mm, v(556.1, 8.51) * mm, v(557.03, 8.55) * mm]});
            skFitSpline(sketch, "E279", {"points": [v(205.91, -20.45) * mm, v(206.02, -20.5) * mm, v(206.13, -20.55) * mm, v(209.08, -21.94) * mm, v(212.14, -23.14) * mm, v(219.72, -25.17) * mm, v(223.07, -26.12) * mm, v(229.73, -27.75) * mm, v(233.03, -28.45) * mm, v(237.85, -29.35) * mm, v(239.34, -29.62) * mm, v(242.32, -30.12) * mm, v(243.8, -30.35) * mm, v(248.24, -31.02) * mm, v(251.2, -31.41) * mm, v(260.04, -32.42) * mm, v(265.9, -32.88) * mm, v(277.44, -33.44) * mm, v(283.1, -33.54) * mm, v(294.51, -33.47) * mm, v(300.28, -33.3) * mm, v(311.66, -32.74) * mm, v(317.27, -32.37) * mm, v(326.3, -31.7) * mm, v(329.7, -31.41) * mm, v(335.63, -30.9) * mm, v(338.14, -30.68) * mm, v(343.16, -30.23) * mm, v(345.67, -30) * mm, v(353.17, -29.26) * mm, v(358.15, -28.73) * mm, v(367.59, -27.65) * mm, v(372.05, -27.1) * mm, v(379.14, -26.15) * mm, v(381.77, -25.78) * mm, v(387.03, -25) * mm, v(389.66, -24.6) * mm, v(397.58, -23.33) * mm, v(402.87, -22.42) * mm, v(413.84, -20.47) * mm, v(419.53, -19.42) * mm, v(429.87, -17.52) * mm, v(434.52, -16.66) * mm, v(443.82, -14.96) * mm, v(448.47, -14.12) * mm, v(462.47, -11.65) * mm, v(471.83, -10.06) * mm, v(485.03, -7.97) * mm, v(488.82, -7.39) * mm, v(496.4, -6.24) * mm, v(500.17, -5.68) * mm, v(511.46, -4) * mm, v(518.94, -2.9) * mm, v(529.5, -1.22) * mm, v(532.62, -0.7) * mm, v(538.87, 0.35) * mm, v(548.62, 1.53) * mm, v(556.33, 2.27) * mm, v(574.18, 5.85) * mm, v(625.6, -5) * mm]});
            skLineSegment(sketch, "E280", {"start": v(262.74, -37.88) * mm, "end": v(261.36, -22.92) * mm});
            skLineSegment(sketch, "E281", {"start": v(261.36, -22.92) * mm, "end": v(251.43, -24.18) * mm});
            skLineSegment(sketch, "E282", {"start": v(251.43, -24.18) * mm, "end": v(252.78, -38.8) * mm});
            skLineSegment(sketch, "E283", {"start": v(422.06, -23.23) * mm, "end": v(420.7, -8.51) * mm});
            skLineSegment(sketch, "E284", {"start": v(420.7, -8.51) * mm, "end": v(410.74, -9.27) * mm});
            skLineSegment(sketch, "E285", {"start": v(410.74, -9.27) * mm, "end": v(412.1, -24.14) * mm});
            skLineSegment(sketch, "E286", {"start": v(415.07, -1.8) * mm, "end": v(417.8, -31.45) * mm});
            skLineSegment(sketch, "E287", {"start": v(255.74, -16.46) * mm, "end": v(258.47, -46.1) * mm});
            skEllipse(sketch, "E288", {"center": v(417.08, -23.68) * mm, "majorRadius": 5 * mm, "minorRadius": 0.85 * mm, "majorAxis": v(1, 0.09)});
            skEllipse(sketch, "E289", {"center": v(257.76, -38.34) * mm, "majorRadius": 5 * mm, "minorRadius": 0.85 * mm, "majorAxis": v(1, 0.09)});
            skArc(sketch, "E290", {"start": v(624.3, -3.41) * mm, "mid": v(591.17, 5.42) * mm, "end": v(557.03, 8.55) * mm});
            skArc(sketch, "E291", {"start": v(622.6, -17.4) * mm, "mid": v(590.35, -8.04) * mm, "end": v(556.96, -4.51) * mm});
            skLineSegment(sketch, "E292", {"start": v(622.1, -19.39) * mm, "end": v(625.57, -5.79) * mm});
            skLineSegment(sketch, "E293", {"start": v(205.91, -20.6) * mm, "end": v(207.17, -34.24) * mm});
            skArc(sketch, "E294", {"start": v(208.41, -18.65) * mm, "mid": v(206.68, -19.01) * mm, "end": v(205.91, -20.6) * mm});
            skArc(sketch, "E295", {"start": v(207.17, -34.24) * mm, "mid": v(207.53, -35.37) * mm, "end": v(208.47, -36.1) * mm});
            skArc(sketch, "E296", {"start": v(625.57, -5.79) * mm, "mid": v(625.4, -4.36) * mm, "end": v(624.3, -3.41) * mm});
            skArc(sketch, "E297", {"start": v(617.36, -22.3) * mm, "mid": v(620.32, -21.8) * mm, "end": v(622.1, -19.39) * mm});
            skLineSegment(sketch, "E298", {"start": v(207.97, -43.06) * mm, "end": v(237.85, -40.27) * mm});
            skLineSegment(sketch, "E299", {"start": v(237.85, -40.27) * mm, "end": v(241.56, -80.1) * mm});
            skLineSegment(sketch, "E300", {"start": v(241.56, -80.1) * mm, "end": v(211.69, -82.88) * mm});
            skLineSegment(sketch, "E301", {"start": v(211.69, -82.88) * mm, "end": v(207.97, -43.06) * mm});
            skLineSegment(sketch, "E302", {"start": v(307.92, -63.19) * mm, "end": v(317.16, -71.9) * mm});
            skCircle(sketch, "E303", {"center": v(286.36, -67.6) * mm, "radius": 5.1 * mm});
            skCircle(sketch, "E304", {"center": v(312.54, -67.54) * mm, "radius": 5.1 * mm});
            skLineSegment(sketch, "E305", {"start": v(316.9, -62.92) * mm, "end": v(308.18, -72.16) * mm});
            skLineSegment(sketch, "E306", {"start": v(432, -22.18) * mm, "end": v(432.4, -26.51) * mm});
            skLineSegment(sketch, "E307", {"start": v(432.36, -31.6) * mm, "end": v(238.72, -49.65) * mm});
            skLineSegment(sketch, "E308", {"start": v(432, -22.18) * mm, "end": v(237.85, -40.27) * mm});
            skArc(sketch, "E309", {"start": v(418.01, -51.52) * mm, "mid": v(429.18, -41.3) * mm, "end": v(432.4, -26.51) * mm});
            skLineSegment(sketch, "E310", {"start": v(432.49, -27.61) * mm, "end": v(238.35, -45.7) * mm});
            skLineSegment(sketch, "E311", {"start": v(262.07, -41.54) * mm, "end": v(262.04, -41.26) * mm});
            skLineSegment(sketch, "E312", {"start": v(254.1, -42.28) * mm, "end": v(254.08, -42) * mm});
            skLineSegment(sketch, "E313", {"start": v(262.07, -41.54) * mm, "end": v(254.1, -42.28) * mm});
            skLineSegment(sketch, "E314", {"start": v(258.14, -42.46) * mm, "end": v(258, -41.08) * mm});
            skLineSegment(sketch, "E315", {"start": v(262.04, -41.26) * mm, "end": v(254.08, -42) * mm});
            skLineSegment(sketch, "E316", {"start": v(262.4, -45.2) * mm, "end": v(262.07, -41.54) * mm});
            skLineSegment(sketch, "E317", {"start": v(254.44, -45.95) * mm, "end": v(254.1, -42.28) * mm});
            skLineSegment(sketch, "E318", {"start": v(281.74, -63.24) * mm, "end": v(290.98, -71.95) * mm});
            skLineSegment(sketch, "E319", {"start": v(290.72, -62.98) * mm, "end": v(282, -72.22) * mm});
            skEllipticalArc(sketch, "E320", {});
            skArc(sketch, "E321", {"start": v(295.37, -91.27) * mm, "mid": v(298.13, -90.95) * mm, "end": v(300.85, -90.47) * mm});
            skArc(sketch, "E322", {"start": v(288.65, -91.7) * mm, "mid": v(292.01, -91.51) * mm, "end": v(295.37, -91.27) * mm});
            skArc(sketch, "E323", {"start": v(300.85, -90.47) * mm, "mid": v(360.53, -74.3) * mm, "end": v(418.01, -51.52) * mm});
            skCircle(sketch, "E324", {"center": v(286.36, -67.6) * mm, "radius": 6.6 * mm});
            skEllipticalArc(sketch, "E325", {});
            skLineSegment(sketch, "E326", {"start": v(262.43, -45.48) * mm, "end": v(262.4, -45.2) * mm});
            skLineSegment(sketch, "E327", {"start": v(254.47, -46.23) * mm, "end": v(254.44, -45.95) * mm});
            skLineSegment(sketch, "E328", {"start": v(262.43, -45.48) * mm, "end": v(254.47, -46.23) * mm});
            skLineSegment(sketch, "E329", {"start": v(258.5, -46.4) * mm, "end": v(258.37, -45.02) * mm});
            skLineSegment(sketch, "E330", {"start": v(262.4, -45.2) * mm, "end": v(254.44, -45.95) * mm});
            skEllipticalArc(sketch, "E331", {});
            skEllipticalArc(sketch, "E332", {});
            skLineSegment(sketch, "E333", {"start": v(421.38, -26.7) * mm, "end": v(421.35, -26.42) * mm});
            skLineSegment(sketch, "E334", {"start": v(413.41, -27.44) * mm, "end": v(413.39, -27.16) * mm});
            skLineSegment(sketch, "E335", {"start": v(421.38, -26.7) * mm, "end": v(413.41, -27.44) * mm});
            skLineSegment(sketch, "E336", {"start": v(417.45, -27.62) * mm, "end": v(417.32, -26.23) * mm});
            skLineSegment(sketch, "E337", {"start": v(421.35, -26.42) * mm, "end": v(413.39, -27.16) * mm});
            skLineSegment(sketch, "E338", {"start": v(421.72, -30.36) * mm, "end": v(421.38, -26.7) * mm});
            skLineSegment(sketch, "E339", {"start": v(413.75, -31.1) * mm, "end": v(413.41, -27.44) * mm});
            skEllipticalArc(sketch, "E340", {});
            skEllipticalArc(sketch, "E341", {});
            skLineSegment(sketch, "E342", {"start": v(421.74, -30.64) * mm, "end": v(421.72, -30.36) * mm});
            skLineSegment(sketch, "E343", {"start": v(413.78, -31.38) * mm, "end": v(413.75, -31.1) * mm});
            skLineSegment(sketch, "E344", {"start": v(421.74, -30.64) * mm, "end": v(413.78, -31.38) * mm});
            skLineSegment(sketch, "E345", {"start": v(417.81, -31.56) * mm, "end": v(417.68, -30.18) * mm});
            skLineSegment(sketch, "E346", {"start": v(421.72, -30.36) * mm, "end": v(413.75, -31.1) * mm});
            skEllipticalArc(sketch, "E347", {});
            skEllipticalArc(sketch, "E348", {});
            skLineSegment(sketch, "E349", {"start": v(241.56, -80.1) * mm, "end": v(237.85, -40.27) * mm});
            skArc(sketch, "E350", {"start": v(284.51, -91.46) * mm, "mid": v(286.57, -91.69) * mm, "end": v(288.65, -91.7) * mm});
            skArc(sketch, "E351", {"start": v(241.56, -80.1) * mm, "mid": v(262.78, -86.74) * mm, "end": v(284.51, -91.46) * mm});
            skCircle(sketch, "E352", {"center": v(286.36, -67.6) * mm, "radius": 5 * mm});
            skLineSegment(sketch, "E353", {"start": v(287.2, -76.56) * mm, "end": v(285.53, -58.63) * mm});
            skLineSegment(sketch, "E354", {"start": v(295.32, -66.76) * mm, "end": v(277.4, -68.43) * mm});
            skLineSegment(sketch, "E355", {"start": v(307.97, -71.96) * mm, "end": v(317.1, -63.13) * mm});
            skCircle(sketch, "E356", {"center": v(311.38, -93.7) * mm, "radius": 5.1 * mm});
            skLineSegment(sketch, "E357", {"start": v(308.12, -62.98) * mm, "end": v(316.95, -72.1) * mm});
            skLineSegment(sketch, "E358", {"start": v(306.81, -98.1) * mm, "end": v(315.94, -89.28) * mm});
            skLineSegment(sketch, "E359", {"start": v(306.96, -89.13) * mm, "end": v(315.8, -98.25) * mm});
            skCircle(sketch, "E360", {"center": v(311.38, -93.7) * mm, "radius": 6.6 * mm});
            skCircle(sketch, "E361", {"center": v(311.38, -93.7) * mm, "radius": 5 * mm});
            skLineSegment(sketch, "E362", {"start": v(320.37, -93.27) * mm, "end": v(302.39, -94.11) * mm});
            skLineSegment(sketch, "E363", {"start": v(310.96, -84.7) * mm, "end": v(311.8, -102.68) * mm});
            const initialGuessF0  = {"E320": [0.25805879099999995, -0.041632746, 3.984779, 0.348624, 0.004, 0.000556692, 3.0717958665604783e-07, 3.1415923071795864], "E325": [0.258084618, -0.0419098909999999, 3.984779, 0.348624, 0.004, 0.000556692, 3.141593, 6.283185], "E331": [0.25842632800000004, -0.045576729999999996, 3.984779, 0.348624, 0.004, 0.000556692, 3.0717958665604783e-07, 3.1415923071795864], "E332": [0.25845215499999996, -0.045853874999999905, 3.984779, 0.348624, 0.004, 0.000556692, 3.141593, 6.283185], "E340": [0.417368482, -0.026786788000000002, 3.984779, 0.348624, 0.004, 0.000556692, 3.0717958665604783e-07, 3.1415923071795864], "E341": [0.4173943089999999, -0.027063932999999908, 3.984779, 0.348624, 0.004, 0.000556692, 3.141593, 6.283185], "E347": [0.41773601900000007, -0.030730772000000003, 3.984779, 0.348624, 0.004, 0.000556692, 3.0717958665604783e-07, 3.1415923071795864], "E348": [0.417761846, -0.031007916999999906, 3.984779, 0.348624, 0.004, 0.000556692, 3.141593, 6.283185]};
            skSetInitialGuess(sketch, initialGuessF0);
            skSolve(sketch);
        }
        {
            var Q0;
            Q0=qCreatedBy(makeId("Right.planeOp"),FACE);
            var sketch = newSketch(context, id + "F1", { "sketchPlane" : qUnion([Q0])});
            skLineSegment(sketch, "E364.0", {"start": v(241.56, -80.1) * mm, "end": v(211.69, -82.88) * mm});
            skLineSegment(sketch, "E364.1", {"start": v(211.69, -82.88) * mm, "end": v(207.97, -43.06) * mm});
            skLineSegment(sketch, "E364.2", {"start": v(207.97, -43.06) * mm, "end": v(237.85, -40.27) * mm});
            skLineSegment(sketch, "E364.3", {"start": v(241.56, -80.1) * mm, "end": v(237.85, -40.27) * mm});
            skSolve(sketch);
        }
        {
            var Q0;
            Q0=qCreatedBy(makeId("Right.planeOp"),FACE);
            var sketch = newSketch(context, id + "F2", { "sketchPlane" : qUnion([Q0])});
            skFitSpline(sketch, "E365.0", {"points": [v(205.91, -20.45) * mm, v(206.02, -20.5) * mm, v(206.13, -20.55) * mm, v(209.08, -21.94) * mm, v(212.14, -23.14) * mm, v(219.72, -25.17) * mm, v(223.07, -26.12) * mm, v(229.73, -27.75) * mm, v(233.03, -28.45) * mm, v(237.85, -29.35) * mm, v(239.34, -29.62) * mm, v(242.32, -30.12) * mm, v(243.8, -30.35) * mm, v(248.24, -31.02) * mm, v(251.2, -31.41) * mm, v(260.04, -32.42) * mm, v(265.9, -32.88) * mm, v(277.44, -33.44) * mm, v(283.1, -33.54) * mm, v(294.51, -33.47) * mm, v(300.28, -33.3) * mm, v(311.66, -32.74) * mm, v(317.27, -32.37) * mm, v(326.3, -31.7) * mm, v(329.7, -31.41) * mm, v(335.63, -30.9) * mm, v(338.14, -30.68) * mm, v(343.16, -30.23) * mm, v(345.67, -30) * mm, v(353.17, -29.26) * mm, v(358.15, -28.73) * mm, v(367.59, -27.65) * mm, v(372.05, -27.1) * mm, v(379.14, -26.15) * mm, v(381.77, -25.78) * mm, v(387.03, -25) * mm, v(389.66, -24.6) * mm, v(397.58, -23.33) * mm, v(402.87, -22.42) * mm, v(413.84, -20.47) * mm, v(419.53, -19.42) * mm, v(429.87, -17.52) * mm, v(434.52, -16.66) * mm, v(443.82, -14.96) * mm, v(448.47, -14.12) * mm, v(462.47, -11.65) * mm, v(471.83, -10.06) * mm, v(485.03, -7.97) * mm, v(488.82, -7.39) * mm, v(496.4, -6.24) * mm, v(500.17, -5.68) * mm, v(511.46, -4) * mm, v(518.94, -2.9) * mm, v(529.5, -1.22) * mm, v(532.62, -0.7) * mm, v(538.87, 0.35) * mm, v(548.62, 1.53) * mm, v(556.33, 2.27) * mm, v(574.18, 5.85) * mm, v(625.6, -5) * mm]});
            skFitSpline(sketch, "E365.2", {"points": [v(208.47, -36.1) * mm, v(217.08, -39.32) * mm, v(243.69, -45.56) * mm, v(285.6, -48.73) * mm, v(336.07, -45.2) * mm, v(385.62, -38.57) * mm, v(435.09, -30.54) * mm, v(484.46, -21.9) * mm, v(525.37, -15.51) * mm, v(557.77, -9.17) * mm, v(617.36, -22.3) * mm]});
            skArc(sketch, "E365.3", {"start": v(207.17, -34.24) * mm, "mid": v(207.53, -35.37) * mm, "end": v(208.47, -36.1) * mm});
            skLineSegment(sketch, "E365.4", {"start": v(622.1, -19.39) * mm, "end": v(625.24, -7.05) * mm});
            skArc(sketch, "E365.5", {"start": v(617.36, -22.3) * mm, "mid": v(620.32, -21.8) * mm, "end": v(622.1, -19.39) * mm});
            skLineSegment(sketch, "E366", {"start": v(207.17, -34.24) * mm, "end": v(206.21, -23.84) * mm});
            skPoint(sketch, "E367.newPointA", {"position": v(205.91, -20.6) * mm});
            skPoint(sketch, "E367.newPointB", {"position": v(205.91, -20.45) * mm});
            skArc(sketch, "E367.filletArc", {"start": v(208.96, -21.8) * mm, "mid": v(207.01, -22.05) * mm, "end": v(206.21, -23.84) * mm});
            skArc(sketch, "E368.filletArc", {"start": v(625.24, -7.05) * mm, "mid": v(625, -5.5) * mm, "end": v(623.71, -4.6) * mm});
            skSolve(sketch);
        }
        {
            var Q0;
            Q0=qCreatedBy(makeId("Right.planeOp"),FACE);
            cPlane(context, id + "F3", {"entities" : qUnion([Q0]), "cplaneType" : CPlaneType.OFFSET, "offset" : 207 * mm, "width" : 150 * mm, "height" : 150 * mm});
        }
        {
            var Q0;
            Q0=sQuery(id+"F2.wireOp",EDGE,"E365.2");
            cPoint(context, id + "F4", {"entities" : qUnion([Q0]), "parameter" : 0.5});
        }
        {
            var Q0;
            Q0=qCreatedBy(makeId("Front.planeOp"),FACE);
            var Q1;
            Q1=qCreatedBy(id+"F4",VERTEX);
            cPlane(context, id + "F5", {"entities" : qUnion([Q0, Q1]), "cplaneType" : CPlaneType.PLANE_POINT, "offset" : 25 * mm, "width" : 150 * mm, "height" : 150 * mm});
        }
        {
            var Q0;
            Q0=qCreatedBy(makeId("Right.planeOp"),FACE);
            var sketch = newSketch(context, id + "F6", { "sketchPlane" : qUnion([Q0])});
            skLineSegment(sketch, "E369.bottom", {"start": v(186.8, -454.74) * mm, "end": v(396.8, -454.74) * mm});
            skLineSegment(sketch, "E369.top", {"start": v(186.8, -448.74) * mm, "end": v(396.8, -448.74) * mm});
            skLineSegment(sketch, "E369.left", {"start": v(186.8, -454.74) * mm, "end": v(186.8, -448.74) * mm});
            skLineSegment(sketch, "E369.right", {"start": v(396.8, -454.74) * mm, "end": v(396.8, -448.74) * mm});
            skSolve(sketch);
        }
        {
            var Q0;
            Q0 = qSketchRegion(id + "F6", true);
            extrude(context, id + "F7", {"entities" : qUnion([Q0]), "endBound" : BoundingType.SYMMETRIC, "depth" : 100 * mm, "offsetDistance" : 25 * mm});
        }
        {
            var Q0;
            Q0=makeQuery(id+"F7.opExtrude","CAP_EDGE",EDGE,{"disambiguationData":[OSD([sQuery(id+"F6.wireOp",EDGE,"E369.left")])],"isStart":false});
            var Q1;
            Q1=makeQuery(id+"F7.opExtrude","CAP_EDGE",EDGE,{"disambiguationData":[OSD([sQuery(id+"F6.wireOp",EDGE,"E369.right")])],"isStart":false});
            var Q2;
            Q2=makeQuery(id+"F7.opExtrude","CAP_EDGE",EDGE,{"disambiguationData":[OSD([sQuery(id+"F6.wireOp",EDGE,"E369.right")])],"isStart":true});
            var Q3;
            Q3=makeQuery(id+"F7.opExtrude","CAP_EDGE",EDGE,{"disambiguationData":[OSD([sQuery(id+"F6.wireOp",EDGE,"E369.left")])],"isStart":true});
            fillet(context, id + "F8", {"entities" : qUnion([Q0, Q1, Q2, Q3]), "radius" : 3 * mm, "tangentPropagation" : true, "allowEdgeOverflow" : false});
        }
        {
            var Q0;
            Q0=makeQuery(id+"F7.opExtrude","SWEPT_FACE",FACE,{"disambiguationData":[OSD([sQuery(id+"F6.wireOp",EDGE,"E369.top")])]});
            var sketch = newSketch(context, id + "F9", { "sketchPlane" : qUnion([Q0])});
            skPoint(sketch, "E370", {"position": v(35, 201.8) * mm});
            skPoint(sketch, "E371", {"position": v(-35, 201.8) * mm});
            skPoint(sketch, "E372", {"position": v(-35, 381.8) * mm});
            skPoint(sketch, "E373", {"position": v(35, 381.8) * mm});
            skSolve(sketch);
        }
        {
            var Q0;
            Q0=sQuery(id+"F9.wireOp",VERTEX,"E370");
            var Q1;
            Q1=sQuery(id+"F9.wireOp",VERTEX,"E371");
            var Q2;
            Q2=sQuery(id+"F9.wireOp",VERTEX,"E373");
            var Q3;
            Q3=sQuery(id+"F9.wireOp",VERTEX,"E372");
            var Q4;
            Q4=makeQuery(id+"F7.opExtrude","SWEPT_BODY",BODY,{"disambiguationData":[OSD([sQuery(id+"F6.wireOp",EDGE,"E369.bottom"),sQuery(id+"F6.wireOp",EDGE,"E369.top"),sQuery(id+"F6.wireOp",EDGE,"E369.left"),sQuery(id+"F6.wireOp",EDGE,"E369.right")])]});
            hole(context, id + "F10", {"style" : HoleStyle.SIMPLE, "endStyle" : HoleEndStyle.THROUGH, "standardTappedOrClearance" : lookupTablePath({ "standard" : "ISO", "size" : "11", "type" : "Drilled" }), "standardBlindInLast" : lookupTablePath({ "standard" : "ISO", "size" : "11", "type" : "Drilled" }), "holeDiameter" : 11 * mm, "majorDiameter" : 5 * mm, "isTappedThrough" : true, "tappedDepth" : 12 * mm, "tapClearance" : 3, "startFromSketch" : true, "locations" : qUnion([Q0, Q1, Q2, Q3]), "scope" : qUnion([Q4])});
        }
        {
            var Q0;
            Q0=qCreatedBy(makeId("Right.planeOp"),FACE);
            var sketch = newSketch(context, id + "F11", { "sketchPlane" : qUnion([Q0])});
            skLineSegment(sketch, "E374.0", {"start": v(260.03, -324.77) * mm, "end": v(260.03, -448.74) * mm});
            skLineSegment(sketch, "E374.1", {"start": v(260.03, -448.74) * mm, "end": v(336.8, -448.74) * mm});
            skLineSegment(sketch, "E374.2", {"start": v(326.86, -416.22) * mm, "end": v(336.8, -448.74) * mm});
            skLineSegment(sketch, "E374.3", {"start": v(331.84, -414.7) * mm, "end": v(326.86, -416.22) * mm});
            skLineSegment(sketch, "E374.4", {"start": v(310.05, -343.46) * mm, "end": v(331.84, -414.7) * mm});
            skLineSegment(sketch, "E374.5", {"start": v(310.05, -343.46) * mm, "end": v(305.08, -344.98) * mm});
            skLineSegment(sketch, "E374.6", {"start": v(297.2, -319.21) * mm, "end": v(305.08, -344.98) * mm});
            skCircle(sketch, "E374.7", {"center": v(279.02, -324.77) * mm, "radius": 4.2 * mm});
            skCircle(sketch, "E374.8", {"center": v(279.03, -435.24) * mm, "radius": 5.1 * mm});
            skPoint(sketch, "E375.orphan", {"position": v(186.8, -448.74) * mm});
            skPoint(sketch, "E376.orphan", {"position": v(396.8, -448.74) * mm});
            skArc(sketch, "E377", {"start": v(297.2, -319.21) * mm, "mid": v(276.23, -305.97) * mm, "end": v(260.03, -324.77) * mm});
            skSolve(sketch);
        }
        {
            var Q0;
            Q0 = qSketchRegion(id + "F11", true);
            extrude(context, id + "F12", {"entities" : qUnion([Q0]), "endBound" : BoundingType.SYMMETRIC, "depth" : 69 * mm, "offsetDistance" : 25 * mm});
        }
        {
            var Q0;
            Q0=makeQuery(id+"F12.opExtrude","CAP_EDGE",EDGE,{"disambiguationData":[OSD([sQuery(id+"F11.wireOp",EDGE,"E374.4")])],"isStart":false});
            var Q1;
            Q1=makeQuery(id+"F12.opExtrude","CAP_EDGE",EDGE,{"disambiguationData":[OSD([sQuery(id+"F11.wireOp",EDGE,"E374.4")])],"isStart":true});
            fillet(context, id + "F13", {"entities" : qUnion([Q0, Q1]), "radius" : 5 * mm, "tangentPropagation" : true, "allowEdgeOverflow" : false});
        }
        {
            var Q0;
            Q0=makeQuery(id+"F12.opExtrude","SWEPT_FACE",FACE,{"disambiguationData":[OSD([sQuery(id+"F11.wireOp",EDGE,"E377")])]});
            var Q1;
            Q1=makeQuery(id+"F12.opExtrude","SWEPT_FACE",FACE,{"disambiguationData":[OSD([sQuery(id+"F11.wireOp",EDGE,"E374.6")])]});
            var Q2;
            Q2=makeQuery(id+"F12.opExtrude","SWEPT_FACE",FACE,{"disambiguationData":[OSD([sQuery(id+"F11.wireOp",EDGE,"E374.2")])]});
            var Q3;
            Q3=makeQuery(id+"F12.opExtrude","SWEPT_FACE",FACE,{"disambiguationData":[OSD([sQuery(id+"F11.wireOp",EDGE,"E374.1")])]});
            var Q4;
            Q4=makeQuery(id+"F12.opExtrude","SWEPT_FACE",FACE,{"disambiguationData":[OSD([sQuery(id+"F11.wireOp",EDGE,"E374.0")])]});
            var Q5;
            Q5=makeQuery(id+"F12.opExtrude","SWEPT_FACE",FACE,{"disambiguationData":[OSD([sQuery(id+"F11.wireOp",EDGE,"E374.8")])]});
            var Q6;
            Q6=makeQuery(id+"F12.opExtrude","SWEPT_FACE",FACE,{"disambiguationData":[OSD([sQuery(id+"F11.wireOp",EDGE,"E374.7")])]});
            var Q7;
            Q7=makeQuery(id+"F12.opExtrude","SWEPT_FACE",FACE,{"disambiguationData":[OSD([sQuery(id+"F11.wireOp",EDGE,"E374.5")])]});
            var Q8;
            Q8=makeQuery(id+"F12.opExtrude","SWEPT_FACE",FACE,{"disambiguationData":[OSD([sQuery(id+"F11.wireOp",EDGE,"E374.3")])]});
            shell(context, id + "F14", {"entities" : qUnion([Q0, Q1, Q2, Q3, Q4, Q5, Q6, Q7, Q8]), "thickness" : 4 * mm});
        }
        {
            var Q0;
            Q0=makeQuery(id+"F12.opExtrude","SWEPT_FACE",FACE,{"disambiguationData":[OSD([sQuery(id+"F11.wireOp",EDGE,"E374.4")])]});
            var sketch = newSketch(context, id + "F15", { "sketchPlane" : qUnion([Q0])});
            skPoint(sketch, "E378", {"position": v(0, -479.6) * mm});
            skPoint(sketch, "E379", {"position": v(0, -433.08) * mm});
            skSolve(sketch);
        }
        {
            var Q0;
            Q0=sQuery(id+"F15.wireOp",VERTEX,"E379");
            var Q1;
            Q1=sQuery(id+"F15.wireOp",VERTEX,"E378");
            var Q2;
            Q2=makeQuery(id+"F12.opExtrude","SWEPT_BODY",BODY,{"disambiguationData":[OSD([sQuery(id+"F11.wireOp",EDGE,"E374.0"),sQuery(id+"F11.wireOp",EDGE,"E374.1"),sQuery(id+"F11.wireOp",EDGE,"E374.2"),sQuery(id+"F11.wireOp",EDGE,"E374.3"),sQuery(id+"F11.wireOp",EDGE,"E374.4"),sQuery(id+"F11.wireOp",EDGE,"E374.5"),sQuery(id+"F11.wireOp",EDGE,"E374.6"),sQuery(id+"F11.wireOp",EDGE,"E374.7"),sQuery(id+"F11.wireOp",EDGE,"E374.8"),sQuery(id+"F11.wireOp",EDGE,"E377")])]});
            hole(context, id + "F16", {"style" : HoleStyle.SIMPLE, "endStyle" : HoleEndStyle.THROUGH, "standardTappedOrClearance" : lookupTablePath({ "standard" : "ISO", "size" : "6.8", "type" : "Drilled" }), "standardBlindInLast" : lookupTablePath({ "standard" : "ISO", "size" : "6.8", "type" : "Drilled" }), "holeDiameter" : 6.8 * mm, "majorDiameter" : 5 * mm, "isTappedThrough" : true, "tappedDepth" : 12 * mm, "tapClearance" : 3, "startFromSketch" : true, "locations" : qUnion([Q0, Q1]), "scope" : qUnion([Q2])});
        }
        {
            var Q0;
            Q0=qCreatedBy(makeId("Right.planeOp"),FACE);
            var sketch = newSketch(context, id + "F17", { "sketchPlane" : qUnion([Q0])});
            skLineSegment(sketch, "E380.0", {"start": v(328.7, -422.64) * mm, "end": v(357.89, -415.72) * mm});
            skLineSegment(sketch, "E380.1", {"start": v(357.89, -415.72) * mm, "end": v(356.97, -411.83) * mm});
            skLineSegment(sketch, "E380.2", {"start": v(356.97, -411.83) * mm, "end": v(327.78, -418.75) * mm});
            skLineSegment(sketch, "E380.3", {"start": v(327.78, -418.75) * mm, "end": v(328.7, -422.64) * mm});
            skLineSegment(sketch, "E380.4", {"start": v(316.38, -405.01) * mm, "end": v(328.31, -421.06) * mm, "construction": true});
            skLineSegment(sketch, "E380.5", {"start": v(328.5, -424.66) * mm, "end": v(315.94, -407.78) * mm, "construction": true});
            skLineSegment(sketch, "E380.6", {"start": v(284.28, -428.88) * mm, "end": v(316.38, -405.01) * mm, "construction": true});
            skLineSegment(sketch, "E380.7", {"start": v(315.94, -407.78) * mm, "end": v(279.03, -435.24) * mm, "construction": true});
            skLineSegment(sketch, "E380.10", {"start": v(323.01, -420.64) * mm, "end": v(317.64, -413.42) * mm, "construction": true});
            skCircle(sketch, "E380.11", {"center": v(279.03, -435.24) * mm, "radius": 8 * mm, "construction": true});
            skCircle(sketch, "E380.12", {"center": v(279.03, -435.24) * mm, "radius": 6 * mm, "construction": true});
            skLineSegment(sketch, "E381", {"start": v(328.31, -421.06) * mm, "end": v(316.38, -405.01) * mm});
            skLineSegment(sketch, "E382", {"start": v(284.28, -428.88) * mm, "end": v(286.67, -432.1) * mm});
            skLineSegment(sketch, "E383", {"start": v(286.67, -432.1) * mm, "end": v(312.75, -412.7) * mm, "construction": true});
            skArc(sketch, "E384", {"start": v(317.64, -413.42) * mm, "mid": v(315.34, -412.04) * mm, "end": v(312.75, -412.7) * mm});
            skLineSegment(sketch, "E385", {"start": v(286.67, -432.1) * mm, "end": v(312.75, -412.7) * mm});
            skLineSegment(sketch, "E386", {"start": v(284.28, -428.88) * mm, "end": v(316.38, -405.01) * mm});
            skLineSegment(sketch, "E387", {"start": v(317.64, -413.42) * mm, "end": v(323.01, -420.64) * mm});
            skArc(sketch, "E388", {"start": v(323.01, -420.64) * mm, "mid": v(325.57, -422.05) * mm, "end": v(328.31, -421.06) * mm});
            skSolve(sketch);
        }
        {
            var Q0;
            Q0 = qSketchRegion(id + "F17", true);
            extrude(context, id + "F18", {"entities" : qUnion([Q0]), "operationType" : NewBodyOperationType.ADD, "endBound" : BoundingType.SYMMETRIC, "depth" : 45 * mm, "offsetDistance" : 25 * mm});
        }
        {
            var Q0;
            Q0=qCreatedBy(makeId("Right.planeOp"),FACE);
            var sketch = newSketch(context, id + "F19", { "sketchPlane" : qUnion([Q0])});
            skCircle(sketch, "E389.0", {"center": v(279.03, -435.24) * mm, "radius": 8 * mm});
            skCircle(sketch, "E389.1", {"center": v(279.03, -435.24) * mm, "radius": 6 * mm});
            skSolve(sketch);
        }
        {
            var Q0;
            Q0 = qSketchRegion(id + "F19", true);
            extrude(context, id + "F20", {"entities" : qUnion([Q0]), "operationType" : NewBodyOperationType.ADD, "endBound" : BoundingType.SYMMETRIC, "depth" : 60 * mm, "offsetDistance" : 25 * mm});
        }
        {
            var Q0;
            Q0=qCreatedBy(makeId("Right.planeOp"),FACE);
            var sketch = newSketch(context, id + "F21", { "sketchPlane" : qUnion([Q0])});
            skLineSegment(sketch, "E390", {"start": v(311.76, -349.04) * mm, "end": v(316.7, -349.8) * mm});
            skLineSegment(sketch, "E391", {"start": v(316.7, -349.8) * mm, "end": v(316.9, -350.43) * mm});
            skLineSegment(sketch, "E392", {"start": v(316.9, -350.43) * mm, "end": v(312.59, -351.74) * mm});
            skLineSegment(sketch, "E393", {"start": v(312.59, -351.74) * mm, "end": v(311.76, -349.04) * mm});
            skLineSegment(sketch, "E394", {"start": v(314.14, -356.83) * mm, "end": v(312.85, -352.6) * mm});
            skLineSegment(sketch, "E395", {"start": v(318.44, -355.5) * mm, "end": v(314.14, -356.83) * mm});
            skPoint(sketch, "E396.visualSharp", {"position": v(315.79, -351.74) * mm});
            skArc(sketch, "E396.filletArc", {"start": v(318.44, -355.5) * mm, "mid": v(316.6, -353.06) * mm, "end": v(313.62, -352.36) * mm});
            skLineSegment(sketch, "E397", {"start": v(312.85, -352.6) * mm, "end": v(313.62, -352.36) * mm});
            skSolve(sketch);
        }
        {
            var Q0;
            Q0=makeQuery(id+"F21.imprint","IMPRINT",FACE,{"disambiguationData":[TD([[makeQuery(id+"F21.imprint","IMPRINT",EDGE,{"derivedFrom":sQuery(id+"F21.wireOp",EDGE,"E394")}),-1.0]])]});
            var Q1;
            Q1=makeQuery(id+"F21.imprint","IMPRINT",FACE,{"disambiguationData":[TD([[makeQuery(id+"F21.imprint","IMPRINT",EDGE,{"derivedFrom":sQuery(id+"F21.wireOp",EDGE,"E390")}),-1.0]])]});
            var Q2;
            Q2=sQuery(id+"F0.wireOp",EDGE,"E51");
            revolve(context, id + "F22", {"operationType" : NewBodyOperationType.ADD, "surfaceOperationType" : NewSurfaceOperationType.NEW, "entities" : qUnion([Q0, Q1]), "axis" : qUnion([Q2]), "revolveType" : RevolveType.FULL});
        }
    });
